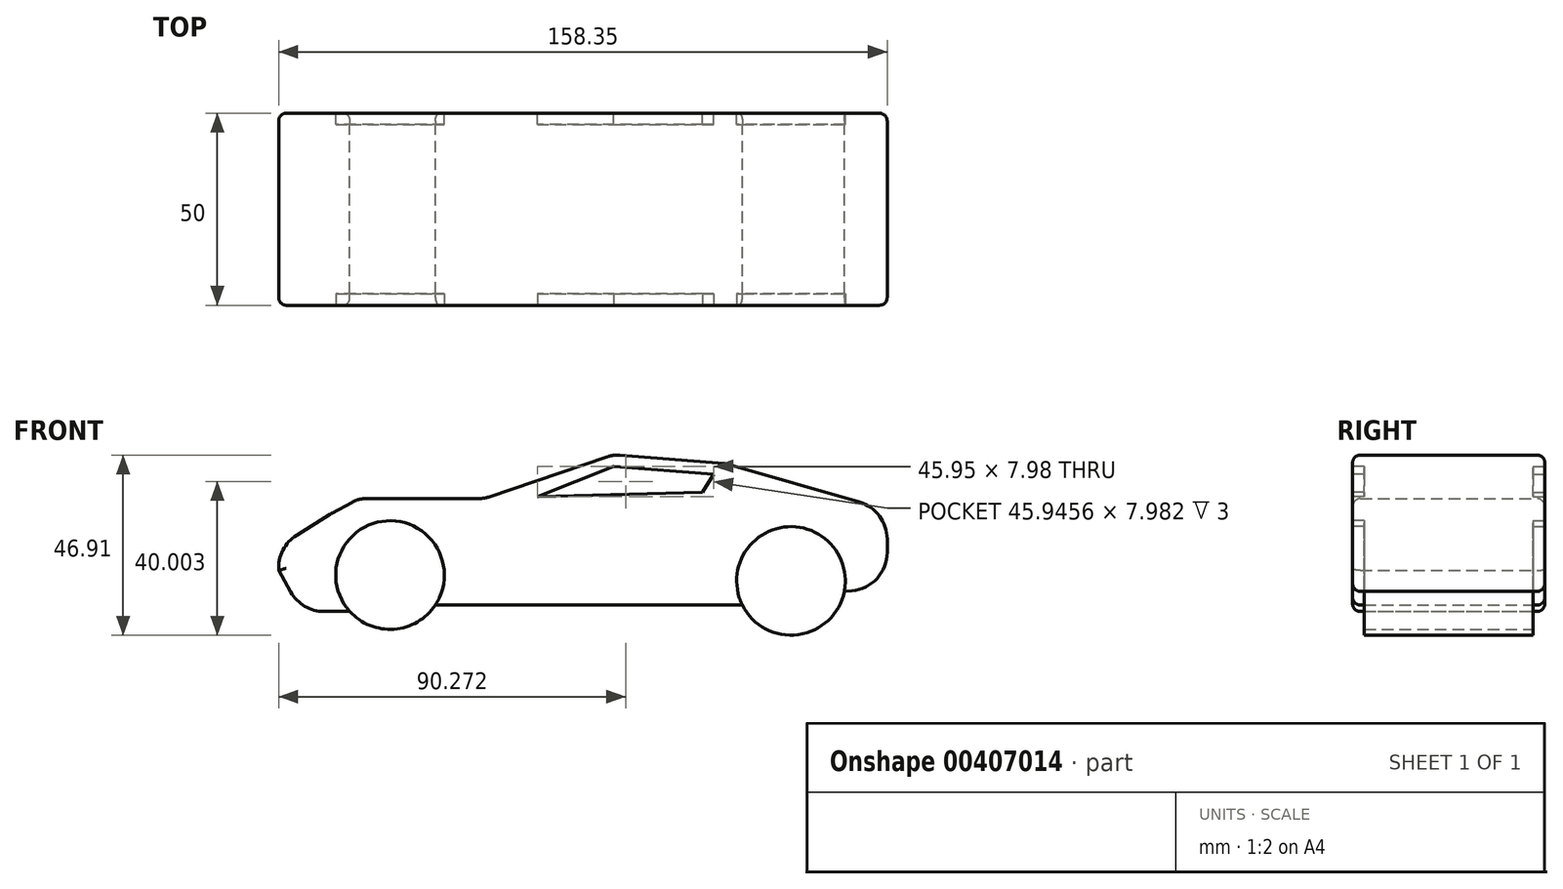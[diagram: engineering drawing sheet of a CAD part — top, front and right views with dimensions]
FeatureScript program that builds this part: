
annotation { "Feature Type Name" : "Feature", "Feature Type Description" : "" }
export const myFeature = defineFeature(function(context is Context, id is Id, definition is map)
    precondition{}
    {
        {
            var Q0;
            Q0=qCreatedBy(makeId("Front.planeOp"),FACE);
            var sketch = newSketch(context, id + "F0", { "sketchPlane" : qUnion([Q0])});
            skArc(sketch, "E0", {"start": v(-68.67, -15.68) * mm, "mid": v(-57.14, -20.27) * mm, "end": v(-46.43, -14) * mm});
            skArc(sketch, "E1", {"start": v(33.48, -14) * mm, "mid": v(48.02, -21.72) * mm, "end": v(60, -10.44) * mm});
            skLineSegment(sketch, "E2", {"start": v(-89.27, 0) * mm, "end": v(-73.58, 9.8) * mm});
            skLineSegment(sketch, "E3", {"start": v(-73.58, 9.8) * mm, "end": v(-66.35, 13.72) * mm});
            skLineSegment(sketch, "E4", {"start": v(-66.35, 13.72) * mm, "end": v(-33.78, 13.72) * mm});
            skLineSegment(sketch, "E5", {"start": v(-33.78, 13.72) * mm, "end": v(0, 25.18) * mm});
            skLineSegment(sketch, "E6", {"start": v(0, 25.18) * mm, "end": v(29.55, 22.77) * mm});
            skLineSegment(sketch, "E7", {"start": v(29.55, 22.77) * mm, "end": v(71.17, 10.7) * mm});
            skLineSegment(sketch, "E8", {"start": v(71.17, 10.7) * mm, "end": v(71.17, -9.5) * mm});
            skLineSegment(sketch, "E9", {"start": v(71.17, -9.5) * mm, "end": v(60, -10.44) * mm});
            skLineSegment(sketch, "E10", {"start": v(33.48, -14) * mm, "end": v(-46.43, -14) * mm});
            skLineSegment(sketch, "E11", {"start": v(-68.67, -15.68) * mm, "end": v(-81.2, -15.68) * mm});
            skLineSegment(sketch, "E12", {"start": v(-81.2, -15.68) * mm, "end": v(-87.15, -4.98) * mm});
            skLineSegment(sketch, "E13", {"start": v(-87.15, -4.98) * mm, "end": v(-89.27, 0) * mm});
            skSolve(sketch);
        }
        {
            var Q0;
            Q0 = qSketchRegion(id + "F0", true);
            extrude(context, id + "F1", {"entities" : qUnion([Q0]), "depth" : 25 * mm});
        }
        {
            var Q0;
            Q0=makeQuery(id+"F1.opExtrude","SWEPT_EDGE",EDGE,{"disambiguationData":[OSD([sQuery(id+"F0.wireOp",EDGE,"E5"),sQuery(id+"F0.wireOp",EDGE,"E6")])]});
            var Q1;
            Q1=makeQuery(id+"F1.opExtrude","SWEPT_EDGE",EDGE,{"disambiguationData":[OSD([sQuery(id+"F0.wireOp",EDGE,"E4"),sQuery(id+"F0.wireOp",EDGE,"E5")])]});
            var Q2;
            Q2=makeQuery(id+"F1.opExtrude","SWEPT_EDGE",EDGE,{"disambiguationData":[OSD([sQuery(id+"F0.wireOp",EDGE,"E3"),sQuery(id+"F0.wireOp",EDGE,"E4")])]});
            var Q3;
            Q3=makeQuery(id+"F1.opExtrude","SWEPT_EDGE",EDGE,{"disambiguationData":[OSD([sQuery(id+"F0.wireOp",EDGE,"E2"),sQuery(id+"F0.wireOp",EDGE,"E3")])]});
            var Q4;
            Q4=makeQuery(id+"F1.opExtrude","SWEPT_EDGE",EDGE,{"disambiguationData":[OSD([sQuery(id+"F0.wireOp",EDGE,"E6"),sQuery(id+"F0.wireOp",EDGE,"E7")])]});
            fillet(context, id + "F2", {"entities" : qUnion([Q0, Q1, Q2, Q3, Q4]), "radius" : 8 * mm, "tangentPropagation" : true, "allowEdgeOverflow" : false});
        }
        {
            var Q0;
            Q0=makeQuery(id+"F1.opExtrude","SWEPT_EDGE",EDGE,{"disambiguationData":[OSD([sQuery(id+"F0.wireOp",EDGE,"E2"),sQuery(id+"F0.wireOp",EDGE,"E13")])]});
            var Q1;
            Q1=makeQuery(id+"F1.opExtrude","SWEPT_EDGE",EDGE,{"disambiguationData":[OSD([sQuery(id+"F0.wireOp",EDGE,"E11"),sQuery(id+"F0.wireOp",EDGE,"E12")])]});
            var Q2;
            Q2=makeQuery(id+"F1.opExtrude","SWEPT_EDGE",EDGE,{"disambiguationData":[OSD([sQuery(id+"F0.wireOp",EDGE,"E7"),sQuery(id+"F0.wireOp",EDGE,"E8")])]});
            var Q3;
            Q3=makeQuery(id+"F1.opExtrude","SWEPT_EDGE",EDGE,{"disambiguationData":[OSD([sQuery(id+"F0.wireOp",EDGE,"E8"),sQuery(id+"F0.wireOp",EDGE,"E9")])]});
            fillet(context, id + "F3", {"entities" : qUnion([Q0, Q1, Q2, Q3]), "radius" : 10 * mm, "tangentPropagation" : true, "allowEdgeOverflow" : false});
        }
        {
            var Q0;
            Q0=makeQuery(id+"F1.opExtrude","CAP_FACE",FACE,{"disambiguationData":[OSD([sQuery(id+"F0.wireOp",EDGE,"E0"),sQuery(id+"F0.wireOp",EDGE,"E1"),sQuery(id+"F0.wireOp",EDGE,"E2"),sQuery(id+"F0.wireOp",EDGE,"E3"),sQuery(id+"F0.wireOp",EDGE,"E4"),sQuery(id+"F0.wireOp",EDGE,"E5"),sQuery(id+"F0.wireOp",EDGE,"E6"),sQuery(id+"F0.wireOp",EDGE,"E7"),sQuery(id+"F0.wireOp",EDGE,"E8"),sQuery(id+"F0.wireOp",EDGE,"E9"),sQuery(id+"F0.wireOp",EDGE,"E10"),sQuery(id+"F0.wireOp",EDGE,"E11"),sQuery(id+"F0.wireOp",EDGE,"E12"),sQuery(id+"F0.wireOp",EDGE,"E13")])],"isStart":false});
            var sketch = newSketch(context, id + "F4", { "sketchPlane" : qUnion([Q0])});
            skLineSegment(sketch, "E14", {"start": v(-19.88, 14.17) * mm, "end": v(0.02, 22.15) * mm});
            skPoint(sketch, "E14.endSnap0", {"position": v(0.02, 25.01) * mm});
            skLineSegment(sketch, "E15", {"start": v(0.02, 22.15) * mm, "end": v(26.06, 20.01) * mm});
            skLineSegment(sketch, "E16", {"start": v(26.06, 20.01) * mm, "end": v(23.14, 15.34) * mm});
            skLineSegment(sketch, "E17", {"start": v(23.14, 15.34) * mm, "end": v(-19.88, 14.17) * mm});
            skCircle(sketch, "E18", {"center": v(-58.2, -6.18) * mm, "radius": 14.13 * mm});
            skCircle(sketch, "E19", {"center": v(46.14, -7.71) * mm, "radius": 14.13 * mm});
            skSolve(sketch);
        }
        {
            var Q0;
            Q0 = qSketchRegion(id + "F4", true);
            extrude(context, id + "F5", {"entities" : qUnion([Q0]), "operationType" : NewBodyOperationType.REMOVE, "oppositeDirection" : true, "depth" : 3 * mm});
        }
        {
            var Q0;
            Q0=makeQuery(id+"F1.opExtrude","CAP_EDGE",EDGE,{"disambiguationData":[OSD([sQuery(id+"F0.wireOp",EDGE,"E11")])],"isStart":false});
            var Q1;
            {var subQ0=sQuery(id+"F0.wireOp",EDGE,"E13");var subQ1=sQuery(id+"F0.wireOp",EDGE,"E2");Q1=makeQuery(id+"F3.opFillet","BLEND_EDGE",EDGE,{"blendedFrom":[makeQuery(id+"F1.opExtrude","SWEPT_EDGE",EDGE,{"disambiguationData":[OSD([subQ1,subQ0])]}),makeQuery(id+"F1.opExtrude","CAP_FACE",FACE,{"disambiguationData":[OSD([sQuery(id+"F0.wireOp",EDGE,"E0"),sQuery(id+"F0.wireOp",EDGE,"E1"),subQ1,sQuery(id+"F0.wireOp",EDGE,"E3"),sQuery(id+"F0.wireOp",EDGE,"E4"),sQuery(id+"F0.wireOp",EDGE,"E5"),sQuery(id+"F0.wireOp",EDGE,"E6"),sQuery(id+"F0.wireOp",EDGE,"E7"),sQuery(id+"F0.wireOp",EDGE,"E8"),sQuery(id+"F0.wireOp",EDGE,"E9"),sQuery(id+"F0.wireOp",EDGE,"E10"),sQuery(id+"F0.wireOp",EDGE,"E11"),sQuery(id+"F0.wireOp",EDGE,"E12"),subQ0])],"isStart":false})],"blendedInto":[makeQuery(id+"F1.opExtrude","CAP_FACE",FACE,{"disambiguationData":[OSD([sQuery(id+"F0.wireOp",EDGE,"E0"),sQuery(id+"F0.wireOp",EDGE,"E1"),subQ1,sQuery(id+"F0.wireOp",EDGE,"E3"),sQuery(id+"F0.wireOp",EDGE,"E4"),sQuery(id+"F0.wireOp",EDGE,"E5"),sQuery(id+"F0.wireOp",EDGE,"E6"),sQuery(id+"F0.wireOp",EDGE,"E7"),sQuery(id+"F0.wireOp",EDGE,"E8"),sQuery(id+"F0.wireOp",EDGE,"E9"),sQuery(id+"F0.wireOp",EDGE,"E10"),sQuery(id+"F0.wireOp",EDGE,"E11"),sQuery(id+"F0.wireOp",EDGE,"E12"),subQ0])],"isStart":false})]});}
            var Q2;
            Q2=makeQuery(id+"F1.opExtrude","CAP_EDGE",EDGE,{"disambiguationData":[OSD([sQuery(id+"F0.wireOp",EDGE,"E2")])],"isStart":false});
            var Q3;
            Q3=makeQuery(id+"F1.opExtrude","CAP_EDGE",EDGE,{"disambiguationData":[OSD([sQuery(id+"F0.wireOp",EDGE,"E10")])],"isStart":false});
            fillet(context, id + "F6", {"entities" : qUnion([Q0, Q1, Q2, Q3]), "radius" : 2 * mm, "tangentPropagation" : true, "allowEdgeOverflow" : false});
        }
        {
            var Q0;
            Q0=makeQuery(id+"F1.opExtrude","SWEPT_BODY",BODY,{"disambiguationData":[OSD([sQuery(id+"F0.wireOp",EDGE,"E0"),sQuery(id+"F0.wireOp",EDGE,"E1"),sQuery(id+"F0.wireOp",EDGE,"E2"),sQuery(id+"F0.wireOp",EDGE,"E3"),sQuery(id+"F0.wireOp",EDGE,"E4"),sQuery(id+"F0.wireOp",EDGE,"E5"),sQuery(id+"F0.wireOp",EDGE,"E6"),sQuery(id+"F0.wireOp",EDGE,"E7"),sQuery(id+"F0.wireOp",EDGE,"E8"),sQuery(id+"F0.wireOp",EDGE,"E9"),sQuery(id+"F0.wireOp",EDGE,"E10"),sQuery(id+"F0.wireOp",EDGE,"E11"),sQuery(id+"F0.wireOp",EDGE,"E12"),sQuery(id+"F0.wireOp",EDGE,"E13")])]});
            var Q1;
            Q1=qCreatedBy(makeId("Front.planeOp"),FACE);
            mirror(context, id + "F7", {"operationType" : NewBodyOperationType.ADD, "entities" : qUnion([Q0]), "mirrorPlane" : qUnion([Q1])});
        }
    });
